FCSTD DOCUMENT  (FreeCAD 0.19R)
Label: mordor
License: All rights reserved
LicenseURL: http://en.wikipedia.org/wiki/All_rights_reserved
objects: App::Link×3, App::DocumentObjectGroup×2, PartDesign::CoordinateSystem×1, App::FeaturePython×1, App::Part×1
note: 1 computed .brp shape members not serialized (recipe doc carries the construction recipe); baked Part::Feature solids carry a one-line shape summary decoded from their .brp
EXTERNAL_REF file=alphacool-xt45-200.FCStd obj=LCS_1
EXTERNAL_REF file=alphacool-xt45-200.FCStd obj=Part
EXTERNAL_REF file=noctua-nf-a20.FCStd obj=LCS_1
EXTERNAL_REF file=noctua-nf-a20.FCStd obj=Part
EXTERNAL_REF file=alphacool-xt45-200.FCStd obj=bottom_fan_mount
EXTERNAL_REF file=noctua-nf-a20.FCStd obj=intake_side_154

FEATURE [App::DocumentObjectGroup] Parts
FEATURE [PartDesign::CoordinateSystem] LCS_Origin
  AttacherType = Attacher::AttachEngine3D
  MapMode = 2
  Support = -> [X_Axis]
FEATURE [App::DocumentObjectGroup] Constraints
FEATURE [App::FeaturePython] Variables  # WARN: FeaturePython — macro-defined, semantics opaque (R4)
FEATURE [App::Link] alphacool_xt45_200_Part
  AssemblyType = Asm4EE
  AttachedBy = #LCS_1
  AttachedTo = Parent Assembly#LCS_Origin
  LinkPlacement = pos=(122.361,-172.936,-20.0881) rot=(1,0,0;1.5708rad)
  LinkedObject = -> <external alphacool-xt45-200.FCStd>#Part
  Placement = pos=(122.361,-172.936,-20.0881) rot=(1,0,0;1.5708rad)
  expr: Placement = LCS_Origin.Placement * AttachmentOffset * alphacool_xt45_200#LCS_1.Placement ^ -1
FEATURE [App::Link] noctua_nf_a20_Part
  AssemblyType = Asm4EE
  AttachedBy = #LCS_1
  AttachedTo = alphacool_xt45_200_Part#LCS_1
  LinkPlacement = pos=(77,-77,0.5) rot=(0.57735,-0.57735,-0.57735;2.0944rad)
  LinkedObject = -> <external noctua-nf-a20.FCStd>#Part
  Placement = pos=(77,-77,0.5) rot=(0.57735,-0.57735,-0.57735;2.0944rad)
  expr: Placement = alphacool_xt45_200_Part.Placement * alphacool_xt45_200#LCS_1.Placement * AttachmentOffset * noctua_nf_a20#LCS_1.Placement ^ -1
FEATURE [App::Link] noctua_nf_a20_Part001
  AssemblyType = Asm4EE
  AttachedBy = #intake_side_154
  AttachedTo = alphacool_xt45_200_Part#bottom_fan_mount
  LinkPlacement = pos=(77,-77,-77) rot=(0.57735,-0.57735,-0.57735;2.0944rad)
  LinkedObject = -> <external noctua-nf-a20.FCStd>#Part
  Placement = pos=(77,-77,-77) rot=(0.57735,-0.57735,-0.57735;2.0944rad)
  expr: Placement = alphacool_xt45_200_Part.Placement * alphacool_xt45_200#bottom_fan_mount.Placement * AttachmentOffset * noctua_nf_a20#intake_side_154.Placement ^ -1
FEATURE [App::Part] Model
  Configuration = 0
  Group = -> [LCS_Origin,Constraints,Variables,alphacool_xt45_200_Part,noctua_nf_a20_Part,noctua_nf_a20_Part001]
  Origin = -> Origin
  Type = Assembly4 Model

RESOLVED EXTERNAL PARTS (link-assembly join: the EXTERNAL_REF files above that resolve inside this repo's crawl, each included once):
---- part alphacool-xt45-200.FCStd = doc fcstd_2f0a278f8837 ----
FCSTD DOCUMENT  (FreeCAD 0.19R)
Label: alphacool-xt45-200
License: All rights reserved
LicenseURL: http://en.wikipedia.org/wiki/All_rights_reserved
objects: PartDesign::CoordinateSystem×2, Part::Feature×1, PartDesign::FeatureBase×1, PartDesign::Body×1, App::Part×1
note: 5 computed .brp shape members not serialized (recipe doc carries the construction recipe); baked Part::Feature solids carry a one-line shape summary decoded from their .brp

FEATURE [Part::Feature] Solid  label="10107-000-Alphacool NexXxoS XT45 Full Copper 200_Shrinkwrap_1"
  shape: bbox 200 x 47 x 239.2 mm, 6627 faces (baked)
FEATURE [PartDesign::CoordinateSystem] LCS_1  label="top-fan-mount"
  AttacherType = Attacher::AttachEngine3D
  AttachmentOffset = pos=(0,0,0) rot=(0,0,-1;1.5708rad)
  MapMode = 11
  Placement = pos=(-122.361,20.0881,-172.936) rot=(-1,0,0;1.5708rad)
  Support = -> [Solid]
FEATURE [PartDesign::FeatureBase] BaseFeature
  BaseFeature = -> Solid
FEATURE [PartDesign::Body] Body
  BaseFeature = -> Solid
  Group = -> [BaseFeature]
  Origin = -> Origin001
  Tip = -> BaseFeature
FEATURE [PartDesign::CoordinateSystem] bottom_fan_mount
  AttacherType = Attacher::AttachEngine3D
  AttachmentOffset = pos=(0,0,-46.5) rot=(0,0,-1;1.5708rad)
  MapMode = 11
  Placement = pos=(-122.361,-26.4119,-172.936) rot=(-1,0,0;1.5708rad)
  Support = -> [BaseFeature]
FEATURE [App::Part] Part
  Group = -> [Body,bottom_fan_mount]
  Origin = -> Origin
